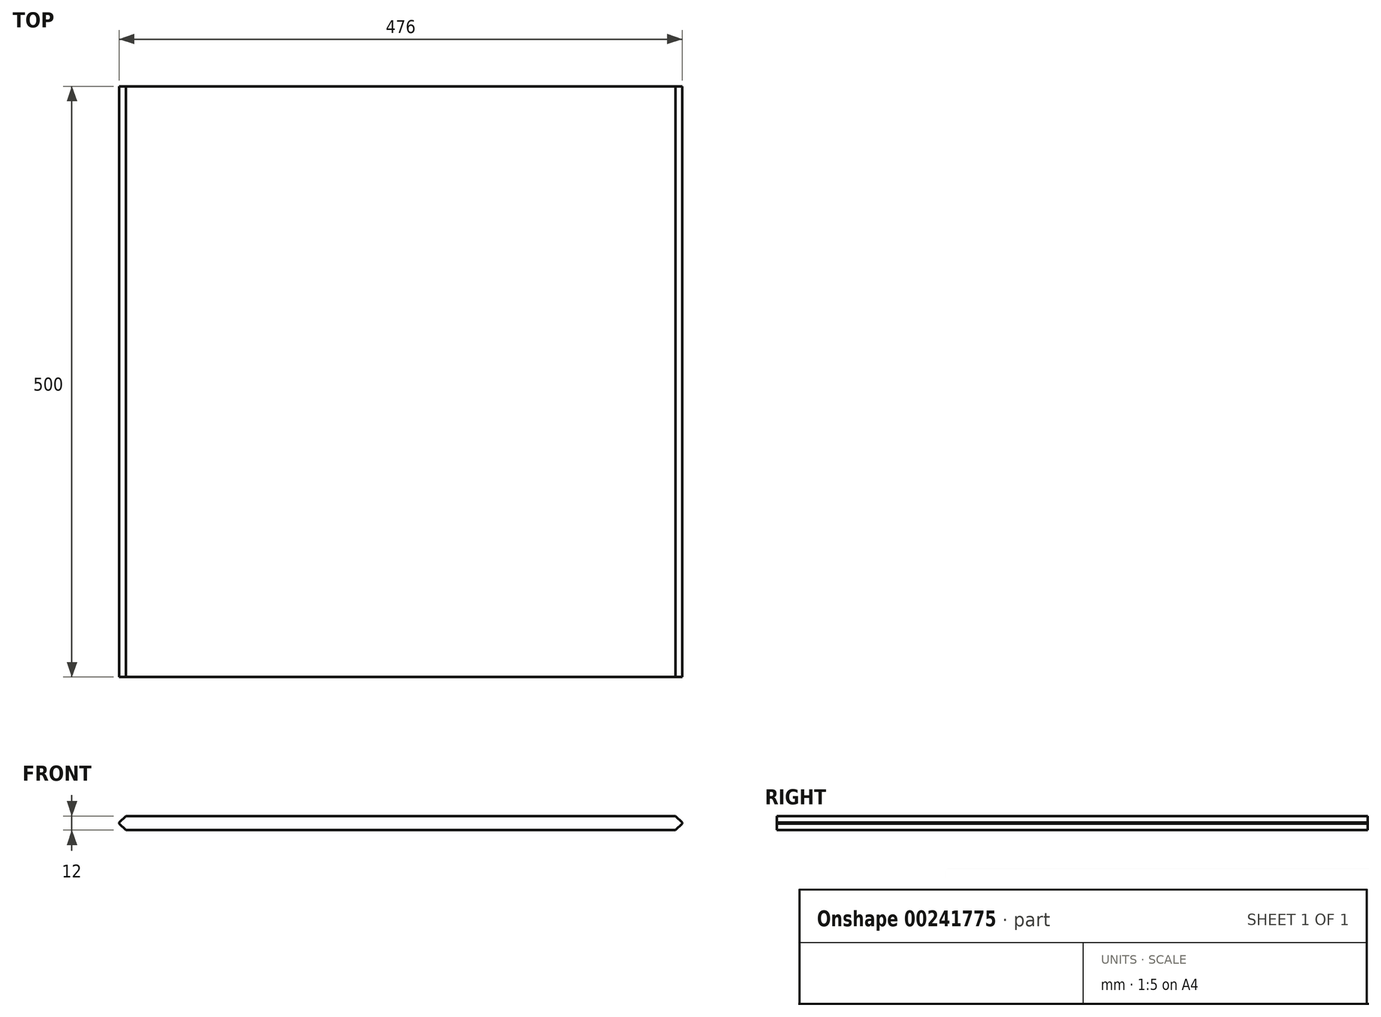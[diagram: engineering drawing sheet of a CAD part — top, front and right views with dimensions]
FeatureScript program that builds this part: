
annotation { "Feature Type Name" : "Feature", "Feature Type Description" : "" }
export const myFeature = defineFeature(function(context is Context, id is Id, definition is map)
    precondition{}
    {
        {
            var Q0;
            Q0=qCreatedBy(makeId("Top.planeOp"),FACE);
            var sketch = newSketch(context, id + "F0", { "sketchPlane" : qUnion([Q0])});
            skLineSegment(sketch, "E0.bottom", {"start": v(0, 0) * mm, "end": v(0, -500) * mm});
            skLineSegment(sketch, "E0.top", {"start": v(476, 0) * mm, "end": v(476, -500) * mm});
            skLineSegment(sketch, "E0.left", {"start": v(0, 0) * mm, "end": v(476, 0) * mm});
            skLineSegment(sketch, "E0.right", {"start": v(0, -500) * mm, "end": v(476, -500) * mm});
            skSolve(sketch);
        }
        {
            var Q0;
            Q0=qSketchRegion(id+"F0",true);
            extrude(context, id + "F1", {"entities" : qUnion([Q0]), "depth" : 12 * mm});
        }
        {
            var Q0;
            Q0=makeQuery(id+"F1.opExtrude","CAP_EDGE",EDGE,{"disambiguationData":[OSD([sQuery(id+"F0.wireOp",EDGE,"E0.top")])],"isStart":false});
            var Q1;
            Q1=makeQuery(id+"F1.opExtrude","CAP_EDGE",EDGE,{"disambiguationData":[OSD([sQuery(id+"F0.wireOp",EDGE,"E0.top")])],"isStart":true});
            var Q2;
            Q2=makeQuery(id+"F1.opExtrude","CAP_EDGE",EDGE,{"disambiguationData":[OSD([sQuery(id+"F0.wireOp",EDGE,"E0.bottom")])],"isStart":false});
            var Q3;
            Q3=makeQuery(id+"F1.opExtrude","CAP_EDGE",EDGE,{"disambiguationData":[OSD([sQuery(id+"F0.wireOp",EDGE,"E0.bottom")])],"isStart":true});
            chamfer(context, id + "F2", {"entities" : qUnion([Q0, Q1, Q2, Q3]), "width" : 5.5 * mm});
        }
    });
